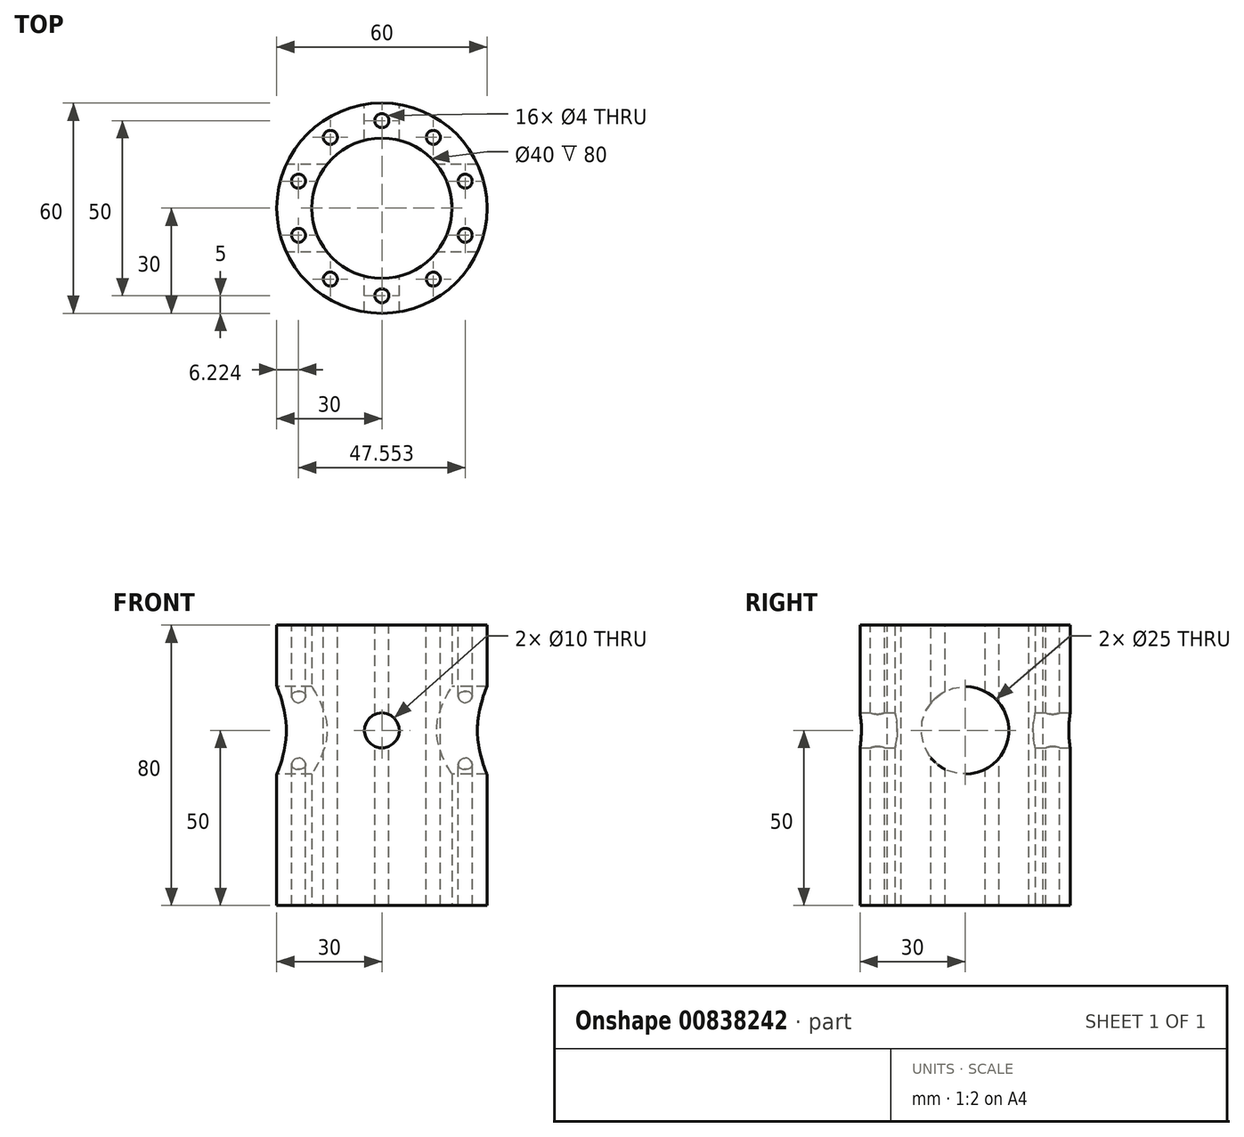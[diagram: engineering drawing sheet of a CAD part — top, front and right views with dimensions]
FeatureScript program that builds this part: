
annotation { "Feature Type Name" : "Feature", "Feature Type Description" : "" }
export const myFeature = defineFeature(function(context is Context, id is Id, definition is map)
    precondition{}
    {
        {
            var Q0;
            Q0=qCreatedBy(makeId("Top.planeOp"),FACE);
            var sketch = newSketch(context, id + "F0", { "sketchPlane" : qUnion([Q0])});
            skCircle(sketch, "E0", {"center": v(0, 0) * mm, "radius": 30 * mm});
            skCircle(sketch, "E1", {"center": v(0, 0) * mm, "radius": 20 * mm});
            skSolve(sketch);
        }
        {
            var Q0;
            Q0 = qSketchRegion(id + "F0", true);
            extrude(context, id + "F1", {"entities" : qUnion([Q0]), "depth" : 80 * mm, "offsetDistance" : 25 * mm});
        }
        {
            var Q0;
            Q0=makeQuery(id+"F1.opExtrude","CAP_FACE",FACE,{"disambiguationData":[OSD([sQuery(id+"F0.wireOp",EDGE,"E0"),sQuery(id+"F0.wireOp",EDGE,"E1")])],"isStart":false});
            var sketch = newSketch(context, id + "F2", { "sketchPlane" : qUnion([Q0])});
            skCircle(sketch, "E2", {"center": v(0, 25) * mm, "radius": 2 * mm});
            skCircle(sketch, "E3.1.0", {"center": v(-14.7, 20.23) * mm, "radius": 2 * mm});
            skCircle(sketch, "E3.2.0", {"center": v(-23.78, 7.73) * mm, "radius": 2 * mm});
            skCircle(sketch, "E3.3.0", {"center": v(-23.78, -7.73) * mm, "radius": 2 * mm});
            skCircle(sketch, "E3.4.0", {"center": v(-14.7, -20.23) * mm, "radius": 2 * mm});
            skCircle(sketch, "E3.5.0", {"center": v(0, -25) * mm, "radius": 2 * mm});
            skCircle(sketch, "E3.6.0", {"center": v(14.7, -20.23) * mm, "radius": 2 * mm});
            skCircle(sketch, "E3.7.0", {"center": v(23.78, -7.73) * mm, "radius": 2 * mm});
            skCircle(sketch, "E3.8.0", {"center": v(23.78, 7.73) * mm, "radius": 2 * mm});
            skCircle(sketch, "E3.9.0", {"center": v(14.7, 20.23) * mm, "radius": 2 * mm});
            skPoint(sketch, "E3.center", {"position": v(0, 0) * mm});
            skSolve(sketch);
        }
        {
            var Q0;
            Q0 = qSketchRegion(id + "F2", true);
            var Q1;
            Q1=makeQuery(id+"F1.opExtrude","CAP_FACE",FACE,{"disambiguationData":[OSD([sQuery(id+"F0.wireOp",EDGE,"E0"),sQuery(id+"F0.wireOp",EDGE,"E1")])],"isStart":true});
            var Q2;
            Q2=makeQuery(id+"F1.opExtrude","CAP_FACE",FACE,{"disambiguationData":[OSD([sQuery(id+"F0.wireOp",EDGE,"E0"),sQuery(id+"F0.wireOp",EDGE,"E1")])],"isStart":true});
            extrude(context, id + "F3", {"entities" : qUnion([Q0, Q1]), "operationType" : NewBodyOperationType.REMOVE, "endBound" : BoundingType.THROUGH_ALL, "oppositeDirection" : true, "depth" : 89.57 * mm, "endBoundEntityFace" : qUnion([Q2]), "offsetDistance" : 25 * mm});
        }
        {
            var Q0;
            Q0=qCreatedBy(makeId("Right.planeOp"),FACE);
            var sketch = newSketch(context, id + "F4", { "sketchPlane" : qUnion([Q0])});
            skCircle(sketch, "E4", {"center": v(0, 50) * mm, "radius": 12.5 * mm});
            skSolve(sketch);
        }
        {
            var Q0;
            Q0 = qSketchRegion(id + "F4", true);
            extrude(context, id + "F5", {"entities" : qUnion([Q0]), "operationType" : NewBodyOperationType.REMOVE, "endBound" : BoundingType.SYMMETRIC, "depth" : 208.98 * mm, "offsetDistance" : 25 * mm});
        }
        {
            var Q0;
            Q0=qCreatedBy(makeId("Front.planeOp"),FACE);
            var sketch = newSketch(context, id + "F6", { "sketchPlane" : qUnion([Q0])});
            skCircle(sketch, "E5", {"center": v(0, 50) * mm, "radius": 5 * mm});
            skSolve(sketch);
        }
        {
            var Q0;
            Q0 = qSketchRegion(id + "F6", true);
            extrude(context, id + "F7", {"entities" : qUnion([Q0]), "operationType" : NewBodyOperationType.REMOVE, "endBound" : BoundingType.SYMMETRIC, "depth" : 120.85 * mm, "offsetDistance" : 25 * mm});
        }
    });
